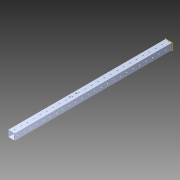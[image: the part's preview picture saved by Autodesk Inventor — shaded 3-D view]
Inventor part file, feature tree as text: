
AUTODESK INVENTOR PART (.ipt)
format: ipt  version: 2014 (Build 180170000, 170)  size: 1,303,552 bytes
history: native  units: in
note: dims shown in document units (in); Inventor stores cm internally (conversion verified against a paired STEP export)
features: extrude x2, sketch x2, pattern_circular x1, other x1, plane x1, imported_body x1, reference x1
ambient origin geometry x8: Origin, YZ Plane, XZ Plane, XY Plane, X Axis, Y Axis, Z Axis, Center Point
bodies: Body1 (feature_tree)
feature tree (9):
  pattern_circular  "CirPattern2"
  other  "217-3426-STEP1"
  plane  "Work Plane1"
  extrude  "Extrusion1"  Depth=3937.0079in TaperAngle=0.0deg
  extrude  "Extrusion7"  [1 undecoded]
  imported_body  "Base1"
  sketch  "Sketch1"  dims[d0=-24.5in d1=3937.0079in d2=0.0in]
  sketch  "Sketch8"  dims[d13=3.937in d14=0.0in]
  reference  "Reference6"
note: 1 required parameter value undecoded (feature->parameter linkage not recoverable at this tier; creation-order binding heuristic only, values carry confidence <= 0.55)
